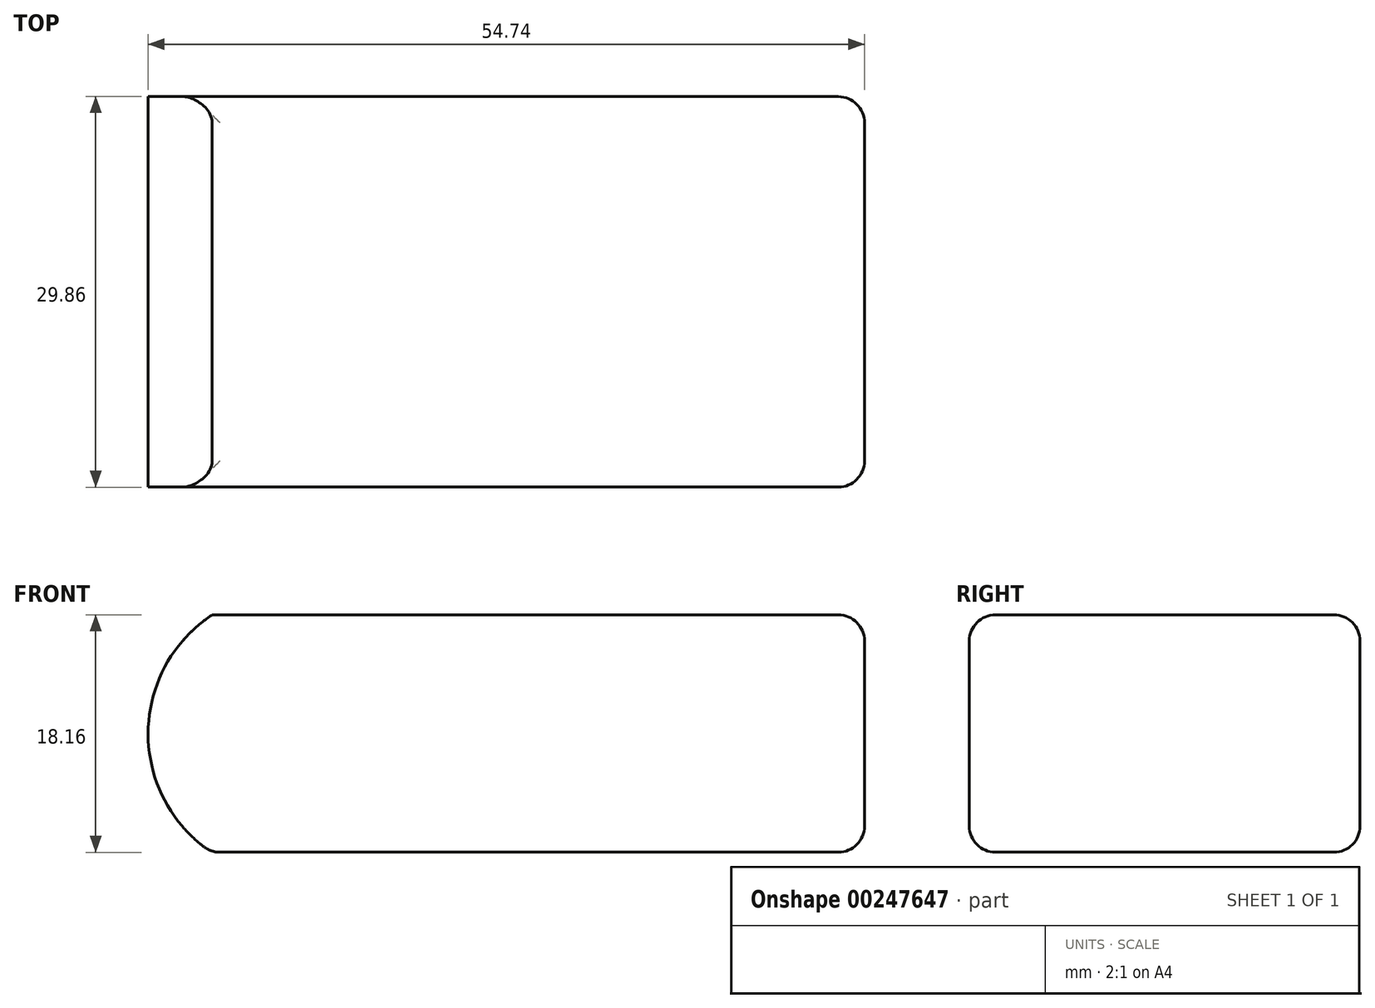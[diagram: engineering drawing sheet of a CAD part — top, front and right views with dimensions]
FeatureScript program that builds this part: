
annotation { "Feature Type Name" : "Feature", "Feature Type Description" : "" }
export const myFeature = defineFeature(function(context is Context, id is Id, definition is map)
    precondition{}
    {
        {
            var Q0;
            Q0=qCreatedBy(makeId("Front.planeOp"),FACE);
            var sketch = newSketch(context, id + "F0", { "sketchPlane" : qUnion([Q0])});
            skLineSegment(sketch, "E0.bottom", {"start": v(27.37, -9.08) * mm, "end": v(-27.37, -9.08) * mm});
            skLineSegment(sketch, "E0.top", {"start": v(27.36, 9.07) * mm, "end": v(-27.37, 9.07) * mm});
            skLineSegment(sketch, "E0.left", {"start": v(27.36, -9.08) * mm, "end": v(27.36, 9.08) * mm});
            skLineSegment(sketch, "E0.right", {"start": v(-27.37, -9.08) * mm, "end": v(-27.37, 9.07) * mm});
            skPoint(sketch, "E0.middle", {"position": v(0, 0) * mm});
            skPoint(sketch, "E1", {"position": v(-27.37, 0) * mm});
            skArc(sketch, "E2", {"start": v(-22.47, 9.07) * mm, "mid": v(-27.36, 0.01) * mm, "end": v(-22.52, -9.08) * mm});
            skText(sketch, "E3", { "text": "Zop power  Li-poly RC battery \n7.4V 25C", "fontName": "OpenSans-Regular.ttf"});
            const initialGuessF0  = {"E3": [0.06, -0.01683, 1, 0, 0.01636]};
            skSetInitialGuess(sketch, initialGuessF0);
            skSolve(sketch);
        }
        {
            var Q0;
            {var subQ4=sQuery(id+"F0.wireOp",EDGE,"E0.left");Q0=makeQuery(id+"F0.imprint","IMPRINT",FACE,{"disambiguationData":[TD([[makeQuery(id+"F0.imprint","IMPRINT",EDGE,{"derivedFrom":subQ4}),1.0]])]});}
            extrude(context, id + "F1", {"entities" : qUnion([Q0]), "depth" : 29.85 * mm, "symmetric" : true});
        }
        {
            var Q0;
            Q0=makeQuery(id+"F1.opExtrude","CAP_EDGE",EDGE,{"disambiguationData":[OSD([sQuery(id+"F0.wireOp",EDGE,"E0.top")])],"isStart":false});
            var Q1;
            Q1=makeQuery(id+"F1.opExtrude","CAP_EDGE",EDGE,{"disambiguationData":[OSD([sQuery(id+"F0.wireOp",EDGE,"E0.top")])],"isStart":true});
            var Q2;
            Q2=makeQuery(id+"F1.opExtrude","SWEPT_EDGE",EDGE,{"disambiguationData":[OSD([sQuery(id+"F0.wireOp",EDGE,"E0.top"),sQuery(id+"F0.wireOp",EDGE,"E0.left")])]});
            var Q3;
            Q3=makeQuery(id+"F1.opExtrude","SWEPT_FACE",FACE,{"disambiguationData":[OSD([sQuery(id+"F0.wireOp",EDGE,"E0.bottom")])]});
            var Q4;
            Q4=makeQuery(id+"F1.opExtrude","CAP_EDGE",EDGE,{"disambiguationData":[OSD([sQuery(id+"F0.wireOp",EDGE,"E0.left")])],"isStart":false});
            var Q5;
            Q5=makeQuery(id+"F1.opExtrude","CAP_EDGE",EDGE,{"disambiguationData":[OSD([sQuery(id+"F0.wireOp",EDGE,"E0.left")])],"isStart":true});
            fillet(context, id + "F2", {"entities" : qUnion([Q0, Q1, Q2, Q3, Q4, Q5]), "radius" : 2 * mm, "tangentPropagation" : true, "allowEdgeOverflow" : false});
        }
    });
